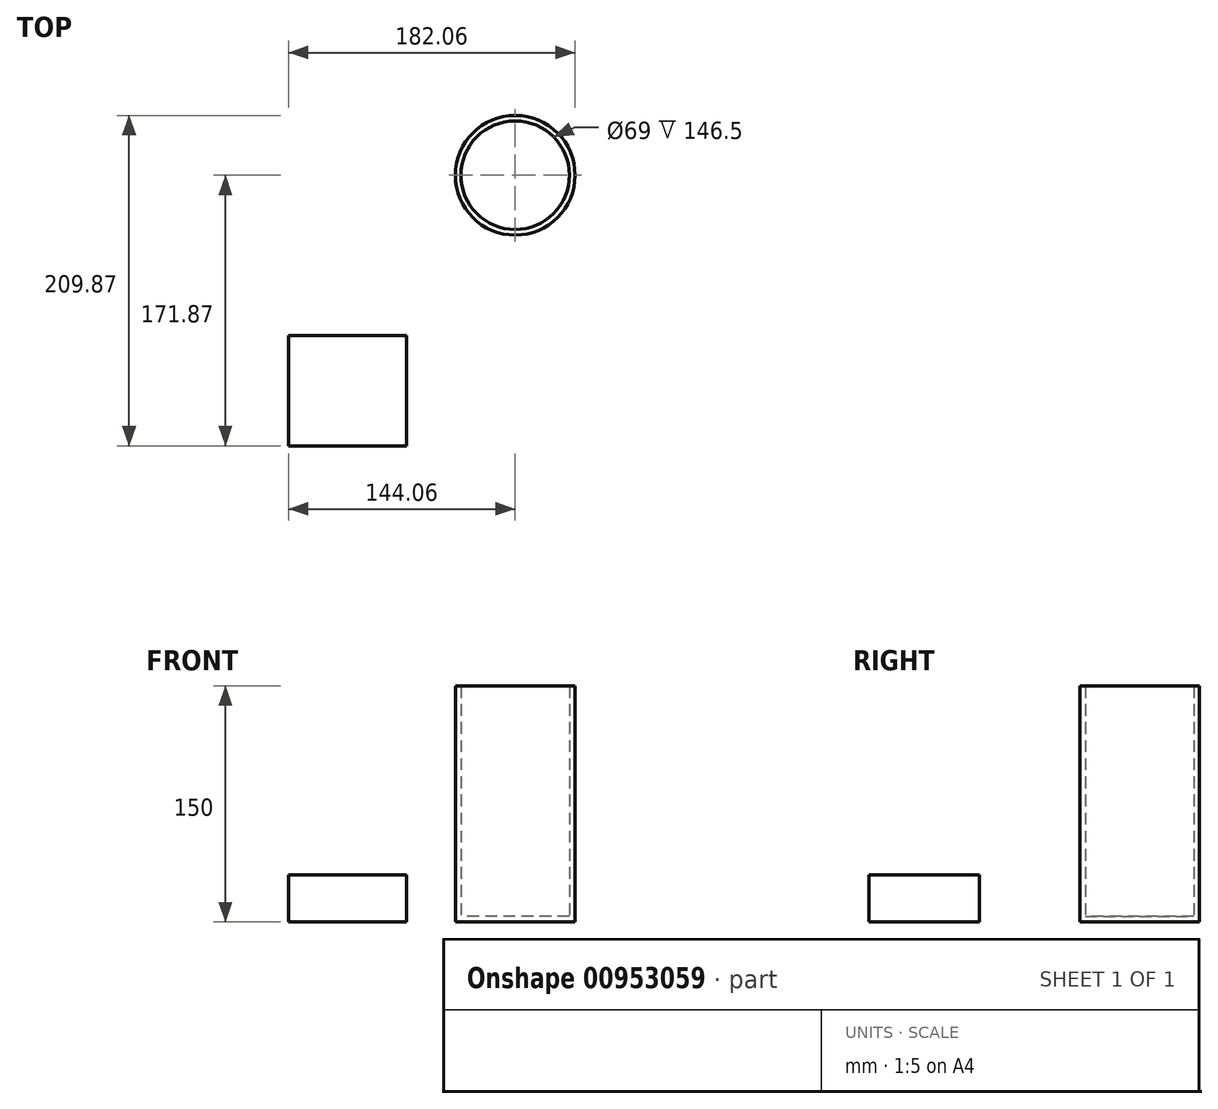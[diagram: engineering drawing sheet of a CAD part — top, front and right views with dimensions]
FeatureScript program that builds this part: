
annotation { "Feature Type Name" : "Feature", "Feature Type Description" : "" }
export const myFeature = defineFeature(function(context is Context, id is Id, definition is map)
    precondition{}
    {
        {
            var Q0;
            Q0=qCreatedBy(makeId("Top.planeOp"),FACE);
            var sketch = newSketch(context, id + "F0", { "sketchPlane" : qUnion([Q0])});
            skCircle(sketch, "E0", {"center": v(0, 0) * mm, "radius": 38 * mm});
            skSolve(sketch);
        }
        {
            var Q0;
            Q0 = qSketchRegion(id + "F0", true);
            extrude(context, id + "F1", {"entities" : qUnion([Q0]), "depth" : 150 * mm, "offsetDistance" : 25 * mm});
        }
        {
            var Q0;
            Q0=makeQuery(id+"F1.opExtrude","CAP_FACE",FACE,{"disambiguationData":[OSD([sQuery(id+"F0.wireOp",EDGE,"E0")])],"isStart":false});
            shell(context, id + "F2", {"entities" : qUnion([Q0]), "thickness" : 3.5 * mm});
        }
        {
            var Q0;
            Q0=qCreatedBy(makeId("Top.planeOp"),FACE);
            var sketch = newSketch(context, id + "F3", { "sketchPlane" : qUnion([Q0])});
            skLineSegment(sketch, "E1.bottom", {"start": v(-69.06, -171.87) * mm, "end": v(-144.06, -171.87) * mm});
            skLineSegment(sketch, "E1.top", {"start": v(-69.06, -101.87) * mm, "end": v(-144.06, -101.87) * mm});
            skLineSegment(sketch, "E1.left", {"start": v(-69.06, -171.87) * mm, "end": v(-69.06, -101.87) * mm});
            skLineSegment(sketch, "E1.right", {"start": v(-144.06, -171.87) * mm, "end": v(-144.06, -101.87) * mm});
            skPoint(sketch, "E1.middle", {"position": v(-106.56, -136.87) * mm});
            skSolve(sketch);
        }
        {
            var Q0;
            Q0=makeQuery(id+"F3.imprint","IMPRINT",FACE,{"disambiguationData":[TD([[makeQuery(id+"F3.imprint","IMPRINT",EDGE,{"derivedFrom":sQuery(id+"F3.wireOp",EDGE,"E1.bottom")}),-1.0]])]});
            extrude(context, id + "F4", {"entities" : qUnion([Q0]), "depth" : 30 * mm, "offsetDistance" : 25 * mm});
        }
    });
